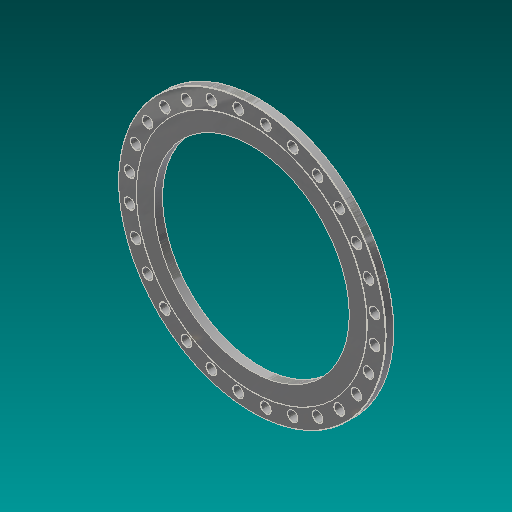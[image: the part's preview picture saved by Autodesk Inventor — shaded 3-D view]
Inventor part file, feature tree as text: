
AUTODESK INVENTOR PART (.ipt)
format: ipt  version: 2017.3 (Build 213257000, 257)  size: 260,608 bytes
history: native  units: in
note: dims shown in document units (in); Inventor stores cm internally (conversion verified against a paired STEP export)
features: chamfer x3, sketch x3, extrude x2, hole x1, pattern_circular x1
ambient origin geometry x8: Origin, YZ Plane, XZ Plane, XY Plane, X Axis, Y Axis, Z Axis, Center Point
bodies: Solid1 (feature_tree)
feature tree (10):
  extrude  "Extrusion1"  Depth=30.5in
  hole  "Hole1"  [1 undecoded]
  chamfer  "Chamfer1"  Distance=11.0236in Angle=360.0deg
  pattern_circular  "Circular Pattern1"  Angle=45.0deg  [1 undecoded]
  chamfer  "Chamfer2"  Distance=0.0625in Angle=45.0deg
  chamfer  "Chamfer4"  Distance=0.0312in Angle=45.0deg
  extrude  "Extrusion3"  Depth=0.0625in
  sketch  "Sketch1"  dims[d0=41.75in d1=30.5in]
  sketch  "Sketch2"  dims[d2=1.3125in d3=0.0in d4=38.5in]
  sketch  "Sketch4"  dims[d5=0.0442in d6=1.625in d7=0.75in d8=0.375in d9=0.25in d10=0.5635in d11=1.0in d12=0.8108in d13=11.0236in d14=360.0deg d16=0.0312in d17=0.125in d18=45.0deg d19=0.0625in d20=0.125in d21=45.0deg d28=0.0312in d29=0.125in d30=45.0deg d31=36.0in d32=0.0625in d33=0.0in]
note: 2 required parameter values undecoded (feature->parameter linkage not recoverable at this tier; creation-order binding heuristic only, values carry confidence <= 0.55)
